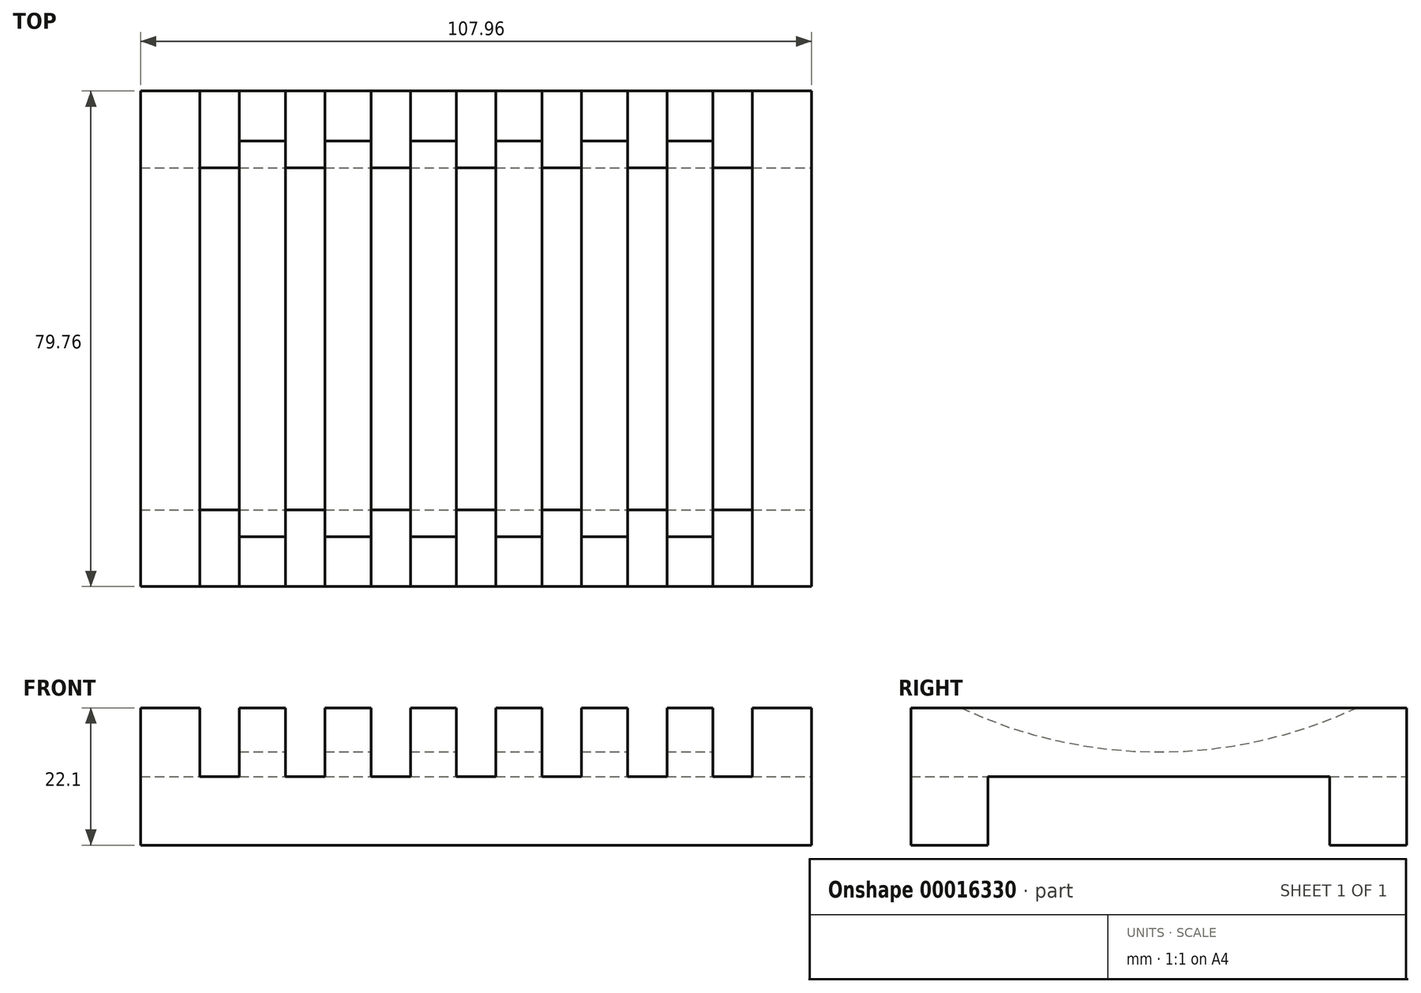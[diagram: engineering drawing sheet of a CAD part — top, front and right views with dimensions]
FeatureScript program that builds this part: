
annotation { "Feature Type Name" : "Feature", "Feature Type Description" : "" }
export const myFeature = defineFeature(function(context is Context, id is Id, definition is map)
    precondition{}
    {
        {
            var Q0;
            Q0=qCreatedBy(makeId("Top.planeOp"),FACE);
            var sketch = newSketch(context, id + "F0", { "sketchPlane" : qUnion([Q0])});
            skLineSegment(sketch, "E0.bottom", {"start": v(-53.98, 39.88) * mm, "end": v(53.97, 39.88) * mm});
            skLineSegment(sketch, "E0.top", {"start": v(-53.98, -39.88) * mm, "end": v(53.97, -39.88) * mm});
            skLineSegment(sketch, "E0.left", {"start": v(-53.98, 39.88) * mm, "end": v(-53.98, -39.88) * mm});
            skLineSegment(sketch, "E0.right", {"start": v(53.97, 39.88) * mm, "end": v(53.97, -39.88) * mm});
            skLineSegment(sketch, "E1", {"start": v(-53.98, 39.88) * mm, "end": v(53.98, -39.88) * mm, "construction": true});
            skSolve(sketch);
        }
        {
            var Q0;
            Q0 = qSketchRegion(id + "F0", true);
            extrude(context, id + "F1", {"entities" : qUnion([Q0]), "depth" : (.87 * 25.4) * mm, "offsetDistance" : 25 * mm});
        }
        {
            var Q0;
            Q0=qCreatedBy(makeId("Right.planeOp"),FACE);
            var sketch = newSketch(context, id + "F2", { "sketchPlane" : qUnion([Q0])});
            skLineSegment(sketch, "E2.bottom", {"start": v(-27.5, 11) * mm, "end": v(27.5, 11) * mm});
            skLineSegment(sketch, "E2.top", {"start": v(-27.5, 0) * mm, "end": v(27.5, 0) * mm});
            skLineSegment(sketch, "E2.left", {"start": v(-27.5, 11) * mm, "end": v(-27.5, 0) * mm});
            skLineSegment(sketch, "E2.right", {"start": v(27.5, 11) * mm, "end": v(27.5, 0) * mm});
            skSolve(sketch);
        }
        {
            var Q0;
            Q0 = qSketchRegion(id + "F2", true);
            extrude(context, id + "F3", {"entities" : qUnion([Q0]), "operationType" : NewBodyOperationType.REMOVE, "endBound" : BoundingType.SYMMETRIC, "oppositeDirection" : true, "depth" : 136.6 * mm, "offsetDistance" : 25 * mm});
        }
        {
            var Q0;
            Q0=qCreatedBy(makeId("Right.planeOp"),FACE);
            var sketch = newSketch(context, id + "F4", { "sketchPlane" : qUnion([Q0])});
            skCircle(sketch, "E3", {"center": v(0, 90) * mm, "radius": 75 * mm});
            skSolve(sketch);
        }
        {
            var Q0;
            Q0 = qSketchRegion(id + "F4", true);
            extrude(context, id + "F5", {"entities" : qUnion([Q0]), "operationType" : NewBodyOperationType.REMOVE, "endBound" : BoundingType.SYMMETRIC, "oppositeDirection" : true, "depth" : (3.5 * 25.4) * mm, "offsetDistance" : 25 * mm});
        }
        {
            var Q0;
            Q0=qCreatedBy(makeId("Front.planeOp"),FACE);
            var sketch = newSketch(context, id + "F6", { "sketchPlane" : qUnion([Q0])});
            skLineSegment(sketch, "E4.bottom", {"start": v(-44.45, 22.1) * mm, "end": v(-38.1, 22.1) * mm});
            skLineSegment(sketch, "E4.top", {"start": v(-44.45, 11) * mm, "end": v(-38.1, 11) * mm});
            skLineSegment(sketch, "E4.left", {"start": v(-44.45, 22.1) * mm, "end": v(-44.45, 11) * mm});
            skLineSegment(sketch, "E4.right", {"start": v(-38.1, 22.1) * mm, "end": v(-38.1, 11) * mm});
            skLineSegment(sketch, "E5.bottom", {"start": v(38.1, 22.1) * mm, "end": v(44.45, 22.1) * mm});
            skLineSegment(sketch, "E5.top", {"start": v(38.1, 11) * mm, "end": v(44.45, 11) * mm});
            skLineSegment(sketch, "E5.left", {"start": v(38.1, 22.1) * mm, "end": v(38.1, 11) * mm});
            skLineSegment(sketch, "E5.right", {"start": v(44.45, 22.1) * mm, "end": v(44.45, 11) * mm});
            skLineSegment(sketch, "E6.1.0.0", {"start": v(-30.69, 22.1) * mm, "end": v(-24.34, 22.1) * mm});
            skLineSegment(sketch, "E6.1.0.1", {"start": v(-30.69, 22.1) * mm, "end": v(-30.69, 11) * mm});
            skLineSegment(sketch, "E6.1.0.2", {"start": v(-24.34, 22.1) * mm, "end": v(-24.34, 11) * mm});
            skLineSegment(sketch, "E6.1.0.3", {"start": v(-30.69, 11) * mm, "end": v(-24.34, 11) * mm});
            skLineSegment(sketch, "E6.2.0.0", {"start": v(-16.93, 22.1) * mm, "end": v(-10.58, 22.1) * mm});
            skLineSegment(sketch, "E6.2.0.1", {"start": v(-16.93, 22.1) * mm, "end": v(-16.93, 11) * mm});
            skLineSegment(sketch, "E6.2.0.2", {"start": v(-10.58, 22.1) * mm, "end": v(-10.58, 11) * mm});
            skLineSegment(sketch, "E6.2.0.3", {"start": v(-16.93, 11) * mm, "end": v(-10.58, 11) * mm});
            skLineSegment(sketch, "E6.3.0.0", {"start": v(-3.17, 22.1) * mm, "end": v(3.18, 22.1) * mm});
            skLineSegment(sketch, "E6.3.0.1", {"start": v(-3.17, 22.1) * mm, "end": v(-3.17, 11) * mm});
            skLineSegment(sketch, "E6.3.0.2", {"start": v(3.18, 22.1) * mm, "end": v(3.18, 11) * mm});
            skLineSegment(sketch, "E6.3.0.3", {"start": v(-3.17, 11) * mm, "end": v(3.18, 11) * mm});
            skLineSegment(sketch, "E6.4.0.0", {"start": v(10.6, 22.1) * mm, "end": v(16.94, 22.1) * mm});
            skLineSegment(sketch, "E6.4.0.1", {"start": v(10.6, 22.1) * mm, "end": v(10.6, 11) * mm});
            skLineSegment(sketch, "E6.4.0.2", {"start": v(16.94, 22.1) * mm, "end": v(16.94, 11) * mm});
            skLineSegment(sketch, "E6.4.0.3", {"start": v(10.6, 11) * mm, "end": v(16.94, 11) * mm});
            skLineSegment(sketch, "E6.5.0.0", {"start": v(24.35, 22.1) * mm, "end": v(30.7, 22.1) * mm});
            skLineSegment(sketch, "E6.5.0.1", {"start": v(24.35, 22.1) * mm, "end": v(24.35, 11) * mm});
            skLineSegment(sketch, "E6.5.0.2", {"start": v(30.7, 22.1) * mm, "end": v(30.7, 11) * mm});
            skLineSegment(sketch, "E6.5.0.3", {"start": v(24.35, 11) * mm, "end": v(30.7, 11) * mm});
            skLineSegment(sketch, "E6.direction1", {"start": v(-44.45, 11) * mm, "end": v(-30.69, 11) * mm, "construction": true});
            skSolve(sketch);
        }
        {
            var Q0;
            Q0 = qSketchRegion(id + "F6", true);
            extrude(context, id + "F7", {"entities" : qUnion([Q0]), "operationType" : NewBodyOperationType.REMOVE, "endBound" : BoundingType.SYMMETRIC, "depth" : 95.8 * mm, "offsetDistance" : 25 * mm});
        }
    });
